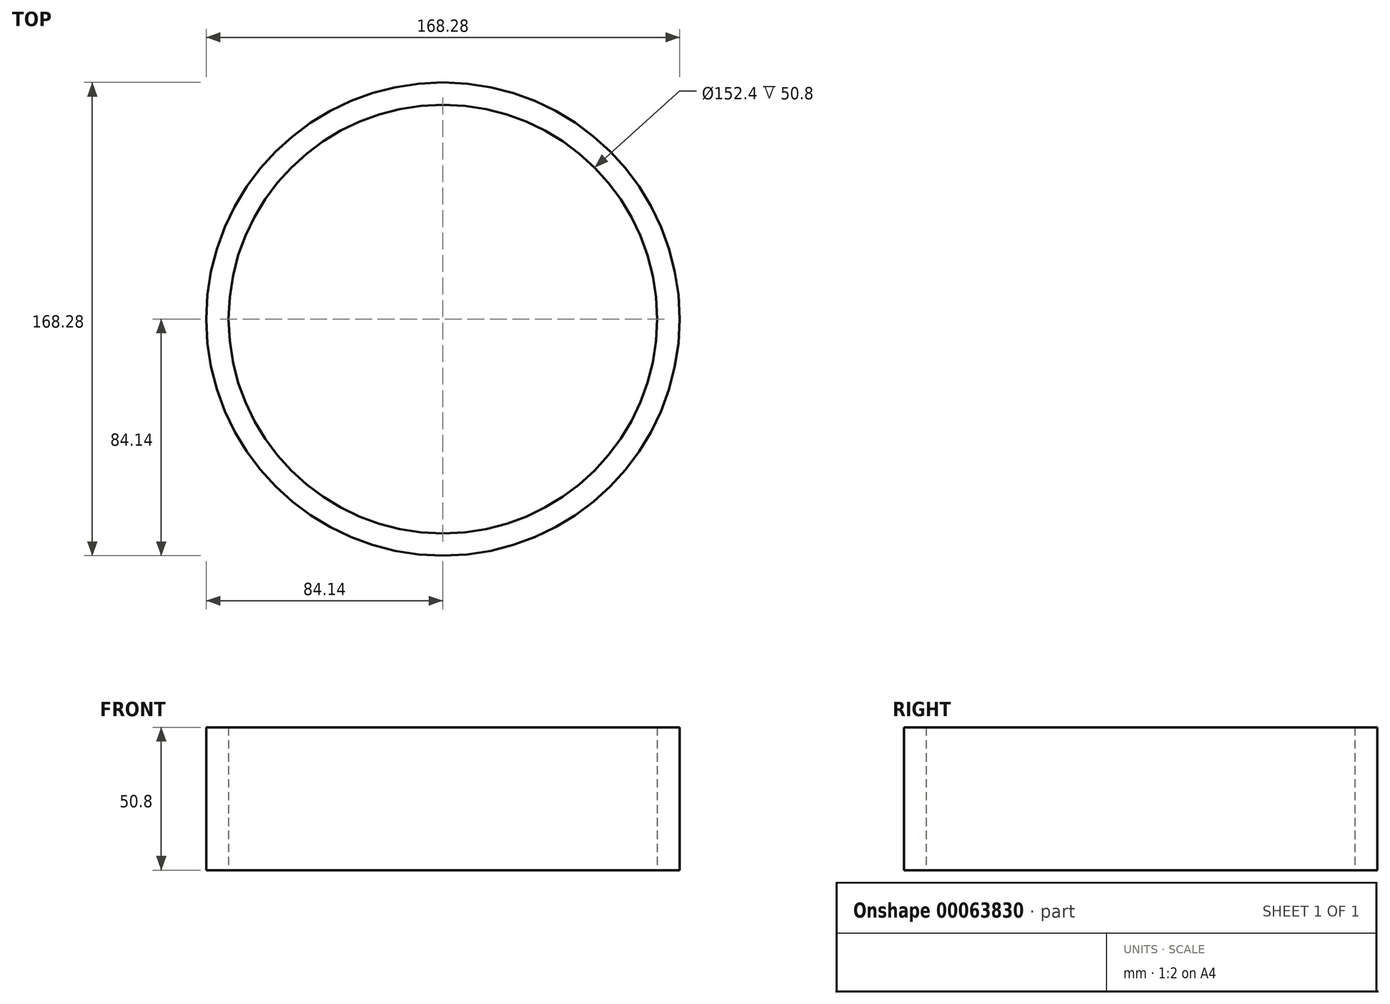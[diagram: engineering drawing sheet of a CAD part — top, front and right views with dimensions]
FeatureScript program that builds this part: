
annotation { "Feature Type Name" : "Feature", "Feature Type Description" : "" }
export const myFeature = defineFeature(function(context is Context, id is Id, definition is map)
    precondition{}
    {
        {
            var Q0;
            Q0=qCreatedBy(makeId("Top.planeOp"),FACE);
            var sketch = newSketch(context, id + "F0", { "sketchPlane" : qUnion([Q0])});
            skCircle(sketch, "E0", {"center": v(0, 0) * mm, "radius": 76.2 * mm});
            skCircle(sketch, "E1", {"center": v(0, 0) * mm, "radius": 84.14 * mm});
            skSolve(sketch);
        }
        {
            var Q0;
            Q0 = qSketchRegion(id + "F0", true);
            extrude(context, id + "F1", {"entities" : qUnion([Q0]), "depth" : 50.8 * mm});
        }
    });
